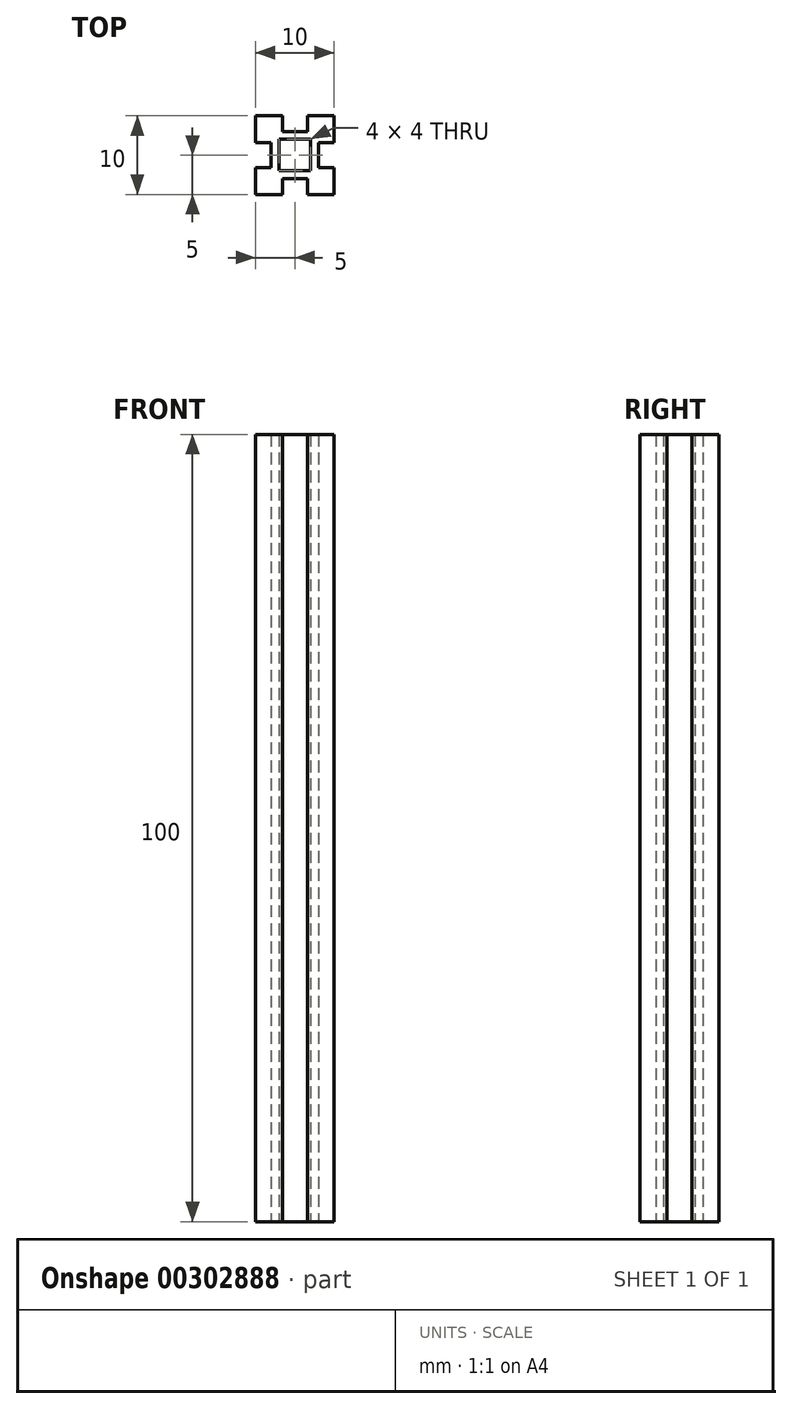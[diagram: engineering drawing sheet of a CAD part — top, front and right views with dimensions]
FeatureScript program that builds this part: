
annotation { "Feature Type Name" : "Feature", "Feature Type Description" : "" }
export const myFeature = defineFeature(function(context is Context, id is Id, definition is map)
    precondition{}
    {
        {
            var Q0;
            Q0=qCreatedBy(makeId("Top.planeOp"),FACE);
            var sketch = newSketch(context, id + "F0", { "sketchPlane" : qUnion([Q0])});
            skLineSegment(sketch, "E0.bottom", {"start": v(5, 5) * mm, "end": v(1.6, 5) * mm});
            skLineSegment(sketch, "E0.right", {"start": v(-5, 5) * mm, "end": v(-5, 1.6) * mm});
            skPoint(sketch, "E0.middle", {"position": v(0, 0) * mm});
            skLineSegment(sketch, "E1.bottom", {"start": v(2, 2) * mm, "end": v(-2, 2) * mm});
            skLineSegment(sketch, "E1.top", {"start": v(2, -2) * mm, "end": v(-2, -2) * mm});
            skLineSegment(sketch, "E1.left", {"start": v(2, 2) * mm, "end": v(2, -2) * mm});
            skLineSegment(sketch, "E1.right", {"start": v(-2, 2) * mm, "end": v(-2, -2) * mm});
            skLineSegment(sketch, "E2", {"start": v(-5, -5) * mm, "end": v(-1.6, -5) * mm});
            skLineSegment(sketch, "E3", {"start": v(5, -5) * mm, "end": v(1.6, -5) * mm});
            skLineSegment(sketch, "E4", {"start": v(-1.6, -5) * mm, "end": v(-1.6, -3) * mm});
            skLineSegment(sketch, "E5", {"start": v(-1.6, -3) * mm, "end": v(1.6, -3) * mm});
            skLineSegment(sketch, "E6", {"start": v(1.6, -3) * mm, "end": v(1.6, -5) * mm});
            skLineSegment(sketch, "E7.MirrorCS", {"start": v(1.6, 3) * mm, "end": v(1.6, 5) * mm});
            skLineSegment(sketch, "E8.MirrorCS", {"start": v(-1.6, 3) * mm, "end": v(1.6, 3) * mm});
            skLineSegment(sketch, "E9.MirrorCS", {"start": v(-1.6, 5) * mm, "end": v(-1.6, 3) * mm});
            skLineSegment(sketch, "E10.trimOffspring", {"start": v(-1.6, 5) * mm, "end": v(-5, 5) * mm});
            skLineSegment(sketch, "E11", {"start": v(5, -5) * mm, "end": v(5, -1.6) * mm});
            skLineSegment(sketch, "E12", {"start": v(5, -1.6) * mm, "end": v(3, -1.6) * mm});
            skLineSegment(sketch, "E13", {"start": v(3, -1.6) * mm, "end": v(3, 1.6) * mm});
            skLineSegment(sketch, "E14", {"start": v(3, 1.6) * mm, "end": v(5, 1.6) * mm});
            skLineSegment(sketch, "E15", {"start": v(5, 1.6) * mm, "end": v(5, 5) * mm});
            skLineSegment(sketch, "E16.MirrorCS", {"start": v(-3, -1.6) * mm, "end": v(-3, 1.6) * mm});
            skLineSegment(sketch, "E17.MirrorCS", {"start": v(-5, -1.6) * mm, "end": v(-3, -1.6) * mm});
            skLineSegment(sketch, "E18.MirrorCS", {"start": v(-3, 1.6) * mm, "end": v(-5, 1.6) * mm});
            skLineSegment(sketch, "E19.trimOffspring", {"start": v(-5, -1.6) * mm, "end": v(-5, -5) * mm});
            skSolve(sketch);
        }
        {
            var Q0;
            Q0=qSketchRegion(id+"F0",true);
            extrude(context, id + "F1", {"entities" : qUnion([Q0]), "depth" : 100 * mm});
        }
    });
